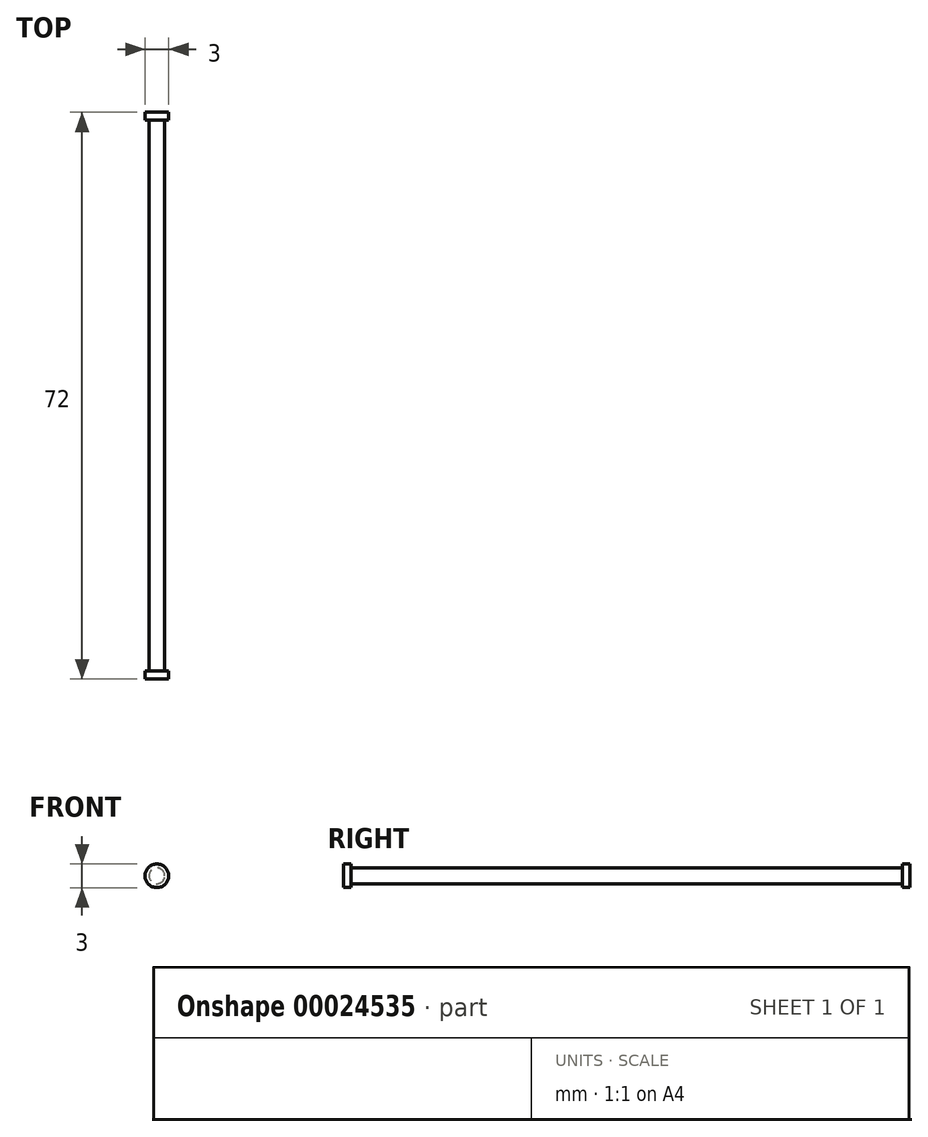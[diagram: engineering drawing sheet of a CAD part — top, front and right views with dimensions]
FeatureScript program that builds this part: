
annotation { "Feature Type Name" : "Feature", "Feature Type Description" : "" }
export const myFeature = defineFeature(function(context is Context, id is Id, definition is map)
    precondition{}
    {
        {
            var Q0;
            Q0=qCreatedBy(makeId("Front.planeOp"),FACE);
            var sketch = newSketch(context, id + "F0", { "sketchPlane" : qUnion([Q0])});
            skCircle(sketch, "E0", {"center": v(-66.29, -9.14) * mm, "radius": 1 * mm});
            skSolve(sketch);
        }
        {
            var Q0;
            Q0 = qSketchRegion(id + "F0", true);
            extrude(context, id + "F1", {"entities" : qUnion([Q0]), "depth" : 70 * mm});
        }
        {
            var Q0;
            Q0=makeQuery(id+"F1.opExtrude","CAP_FACE",FACE,{"disambiguationData":[OSD([sQuery(id+"F0.wireOp",EDGE,"E0")])],"isStart":false});
            var sketch = newSketch(context, id + "F2", { "sketchPlane" : qUnion([Q0])});
            skCircle(sketch, "E1", {"center": v(-66.29, -9.14) * mm, "radius": 1.5 * mm});
            skSolve(sketch);
        }
        {
            var Q0;
            Q0 = qSketchRegion(id + "F2", true);
            extrude(context, id + "F3", {"entities" : qUnion([Q0]), "operationType" : NewBodyOperationType.ADD, "depth" : 1 * mm});
        }
        {
            var Q0;
            Q0=makeQuery(id+"F1.opExtrude","CAP_FACE",FACE,{"disambiguationData":[OSD([sQuery(id+"F0.wireOp",EDGE,"E0")])],"isStart":true});
            var sketch = newSketch(context, id + "F4", { "sketchPlane" : qUnion([Q0])});
            skCircle(sketch, "E2", {"center": v(66.29, -9.14) * mm, "radius": 1.5 * mm});
            skSolve(sketch);
        }
        {
            var Q0;
            Q0 = qSketchRegion(id + "F4", true);
            extrude(context, id + "F5", {"entities" : qUnion([Q0]), "operationType" : NewBodyOperationType.ADD, "depth" : 1 * mm});
        }
    });
